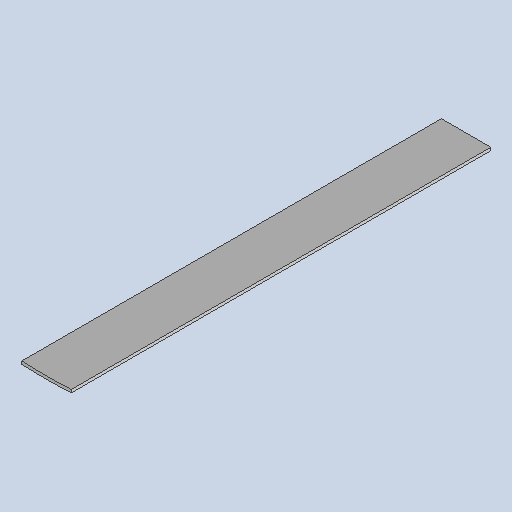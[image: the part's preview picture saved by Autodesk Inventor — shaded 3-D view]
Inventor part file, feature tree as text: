
AUTODESK INVENTOR PART (.ipt)
format: ipt  version: 2025 (Build 290162010, 162A)  size: 270,848 bytes
history: native  units: mm
features: other x3, sheet_metal_op x1, sketch x1
ambient origin geometry x8: Origin, YZ Plane, XZ Plane, XY Plane, X Axis, Y Axis, Z Axis, Center Point
bodies: Body1 (feature_tree)
feature tree (5):
  other  "BSH 504 inner cross"
  sheet_metal_op  "Face2"
  sketch  "Sketch1"  dims[d11=1100.0mm d12=900.0mm d13=25.0mm d14=25.0mm d15=3.0mm d16=25.0mm]
  other  "Plate2"
  other  "Definition1"
